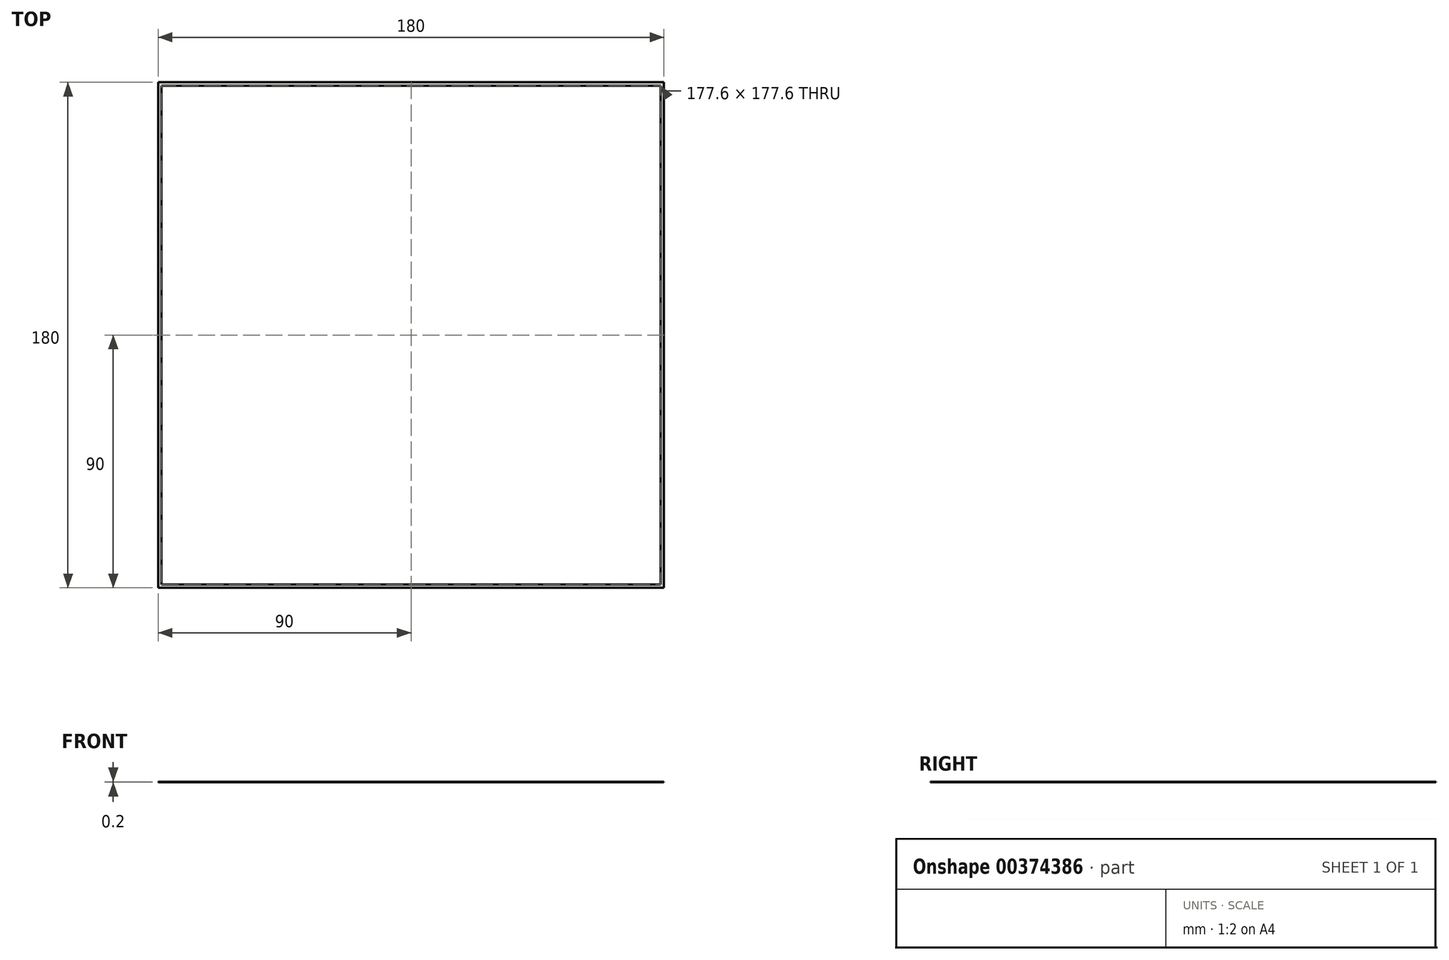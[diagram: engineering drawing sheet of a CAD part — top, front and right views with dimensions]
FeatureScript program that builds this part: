
annotation { "Feature Type Name" : "Feature", "Feature Type Description" : "" }
export const myFeature = defineFeature(function(context is Context, id is Id, definition is map)
    precondition{}
    {
        {
            var Q0;
            Q0=qCreatedBy(makeId("Top.planeOp"),FACE);
            var sketch = newSketch(context, id + "F0", { "sketchPlane" : qUnion([Q0])});
            skLineSegment(sketch, "E0.bottom", {"start": v(0, 0) * mm, "end": v(180, 0) * mm});
            skLineSegment(sketch, "E0.top", {"start": v(0, 180) * mm, "end": v(180, 180) * mm});
            skLineSegment(sketch, "E0.left", {"start": v(0, 0) * mm, "end": v(0, 180) * mm});
            skLineSegment(sketch, "E0.right", {"start": v(180, 0) * mm, "end": v(180, 180) * mm});
            skLineSegment(sketch, "E1.0", {"start": v(178.8, 1.2) * mm, "end": v(178.8, 178.8) * mm});
            skLineSegment(sketch, "E1.1", {"start": v(1.2, 1.2) * mm, "end": v(178.8, 1.2) * mm});
            skLineSegment(sketch, "E1.2", {"start": v(1.2, 1.2) * mm, "end": v(1.2, 178.8) * mm});
            skLineSegment(sketch, "E1.3", {"start": v(1.2, 178.8) * mm, "end": v(178.8, 178.8) * mm});
            skSolve(sketch);
        }
        {
            var Q0;
            Q0=makeQuery(id+"F0.imprint","IMPRINT",FACE,{"disambiguationData":[TD([[makeQuery(id+"F0.imprint","IMPRINT",EDGE,{"derivedFrom":sQuery(id+"F0.wireOp",EDGE,"E0.bottom")}),1.0]])]});
            extrude(context, id + "F1", {"entities" : qUnion([Q0]), "depth" : .2 * mm});
        }
    });
